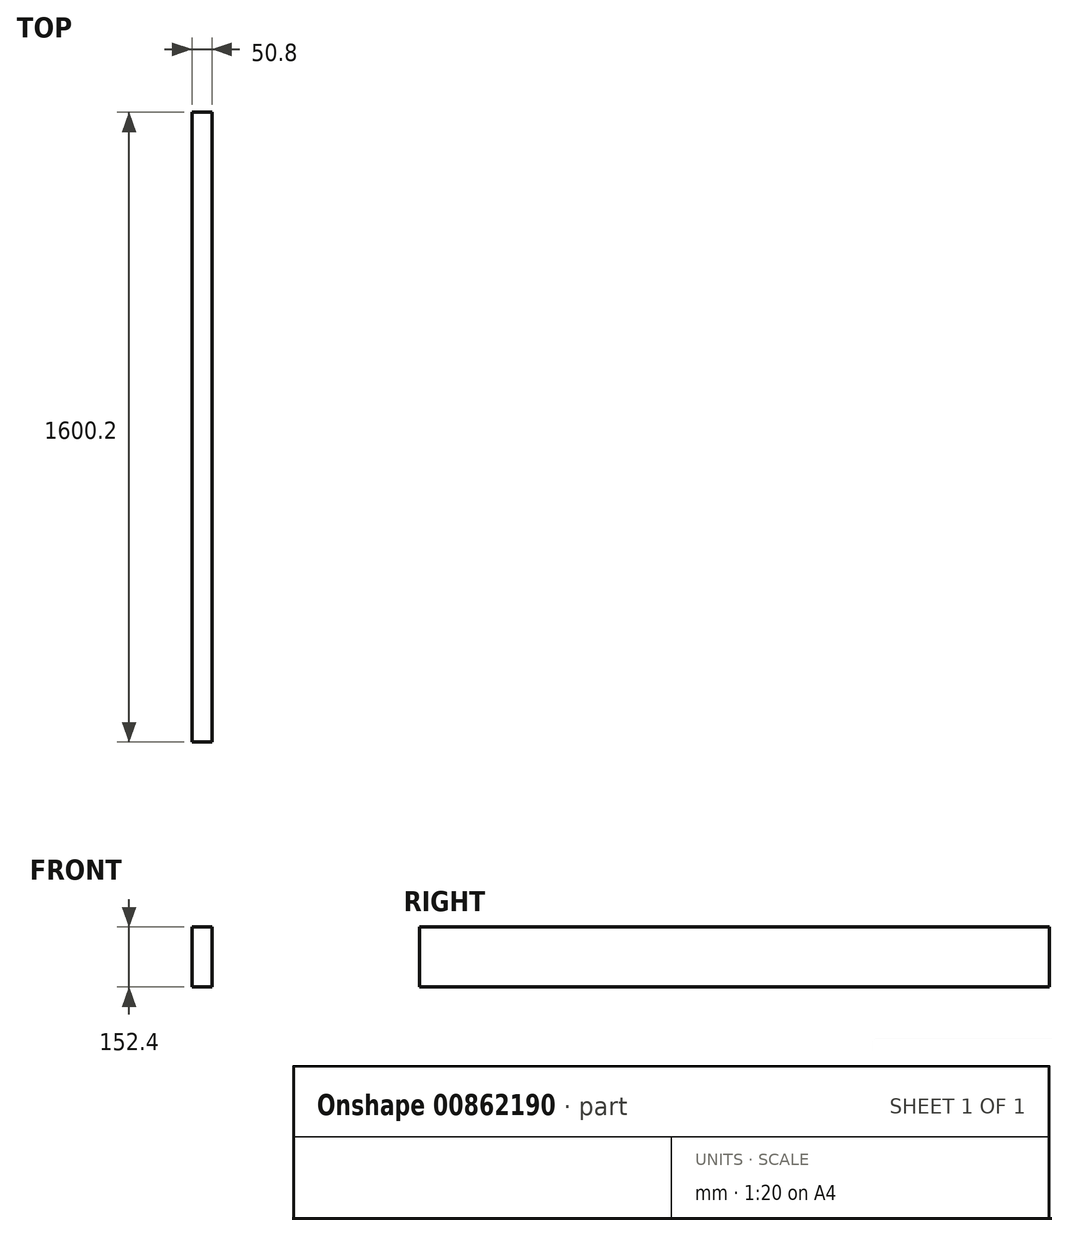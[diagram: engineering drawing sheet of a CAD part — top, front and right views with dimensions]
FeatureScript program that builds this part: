
annotation { "Feature Type Name" : "Feature", "Feature Type Description" : "" }
export const myFeature = defineFeature(function(context is Context, id is Id, definition is map)
    precondition{}
    {
        {
            var Q0;
            Q0=qCreatedBy(makeId("Right.planeOp"),FACE);
            var sketch = newSketch(context, id + "F0", { "sketchPlane" : qUnion([Q0])});
            skLineSegment(sketch, "E0.bottom", {"start": v(-219.36, 0) * mm, "end": v(1380.84, 0) * mm});
            skLineSegment(sketch, "E0.top", {"start": v(-219.36, 152.4) * mm, "end": v(1380.84, 152.4) * mm});
            skLineSegment(sketch, "E0.left", {"start": v(-219.36, 0) * mm, "end": v(-219.36, 152.4) * mm});
            skLineSegment(sketch, "E0.right", {"start": v(1380.84, 0) * mm, "end": v(1380.84, 152.4) * mm});
            skSolve(sketch);
        }
        {
            var Q0;
            Q0=makeQuery(id+"F0.imprint","IMPRINT",FACE,{"disambiguationData":[TD([[makeQuery(id+"F0.imprint","IMPRINT",EDGE,{"derivedFrom":sQuery(id+"F0.wireOp",EDGE,"E0.bottom")}),1.0]])]});
            extrude(context, id + "F1", {"entities" : qUnion([Q0]), "depth" : 50.8 * mm, "offsetDistance" : 25.4 * mm});
        }
    });
